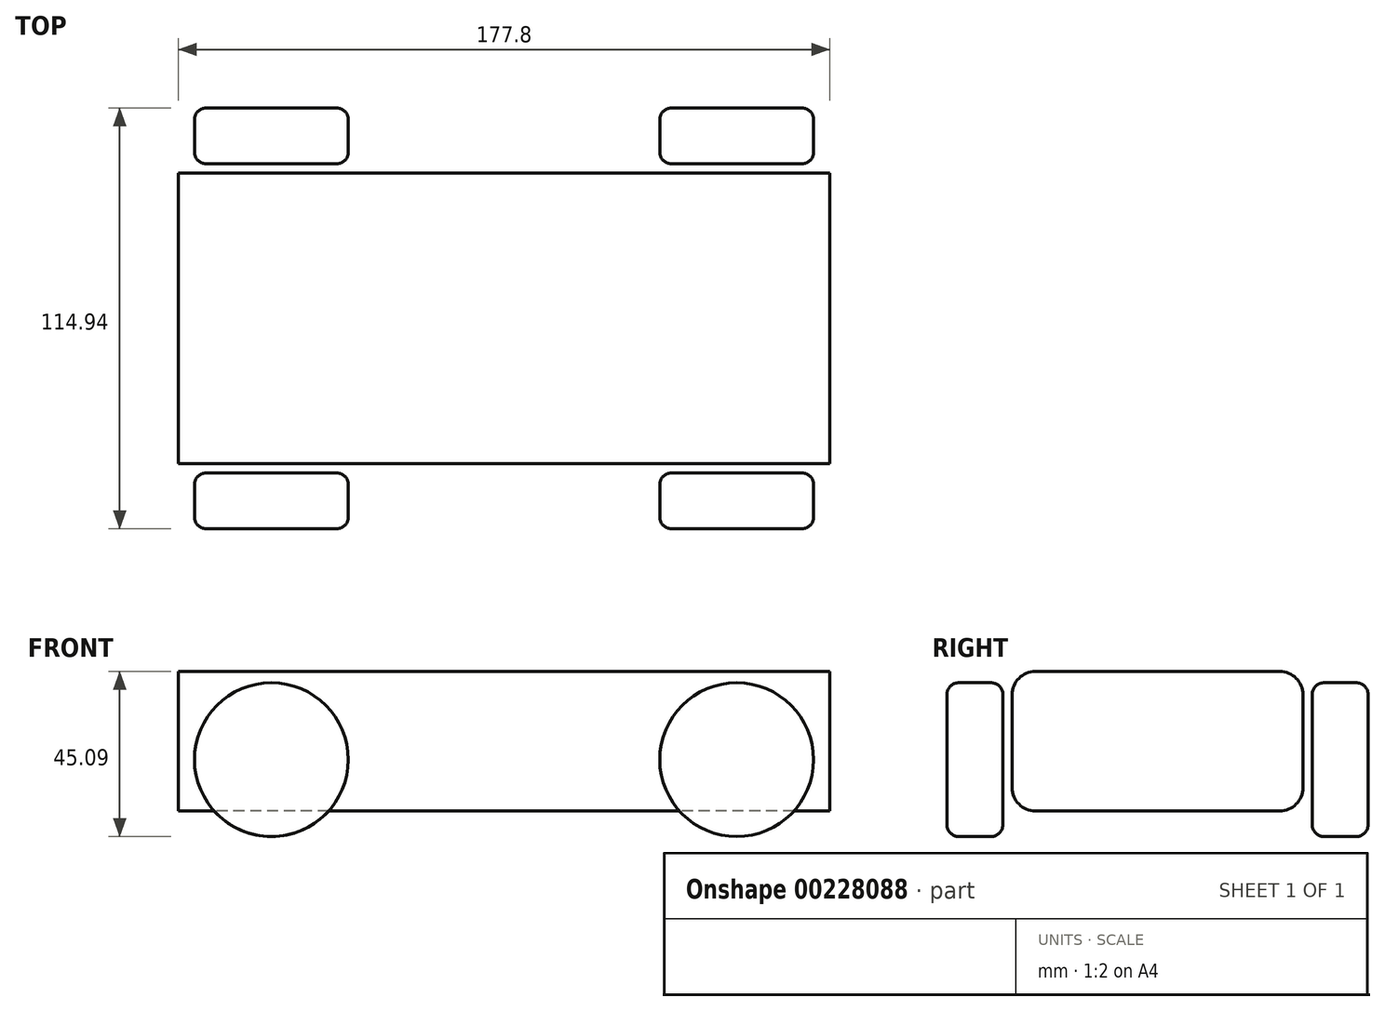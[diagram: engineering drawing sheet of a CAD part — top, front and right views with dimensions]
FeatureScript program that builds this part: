
annotation { "Feature Type Name" : "Feature", "Feature Type Description" : "" }
export const myFeature = defineFeature(function(context is Context, id is Id, definition is map)
    precondition{}
    {
        {
            var Q0;
            Q0=qCreatedBy(makeId("Front.planeOp"),FACE);
            var sketch = newSketch(context, id + "F0", { "sketchPlane" : qUnion([Q0])});
            skLineSegment(sketch, "E0.bottom", {"start": v(88.9, 19.05) * mm, "end": v(-88.9, 19.05) * mm});
            skLineSegment(sketch, "E0.top", {"start": v(88.9, -19.05) * mm, "end": v(-88.9, -19.05) * mm});
            skLineSegment(sketch, "E0.left", {"start": v(88.9, 19.05) * mm, "end": v(88.9, -19.05) * mm});
            skLineSegment(sketch, "E0.right", {"start": v(-88.9, 19.05) * mm, "end": v(-88.9, -19.05) * mm});
            skPoint(sketch, "E0.middle", {"position": v(0, 0) * mm});
            skLineSegment(sketch, "E1", {"start": v(-95.98, -26.04) * mm, "end": v(99.46, -26.03) * mm, "construction": true});
            skCircle(sketch, "E2", {"center": v(63.5, -5.03) * mm, "radius": 21 * mm});
            skSolve(sketch);
        }
        {
            var Q0;
            Q0=qCreatedBy(makeId("Front.planeOp"),FACE);
            var sketch = newSketch(context, id + "F1", { "sketchPlane" : qUnion([Q0])});
            skLineSegment(sketch, "E3.0", {"start": v(88.9, 19.05) * mm, "end": v(-88.9, 19.05) * mm});
            skLineSegment(sketch, "E4.0", {"start": v(-88.9, 19.05) * mm, "end": v(-88.9, -19.05) * mm});
            skLineSegment(sketch, "E5.0", {"start": v(88.9, -19.05) * mm, "end": v(-88.9, -19.05) * mm});
            skLineSegment(sketch, "E6.0", {"start": v(88.9, 19.05) * mm, "end": v(88.9, -19.05) * mm});
            skSolve(sketch);
        }
        {
            var Q0;
            Q0 = qSketchRegion(id + "F1", true);
            extrude(context, id + "F2", {"entities" : qUnion([Q0]), "endBound" : BoundingType.SYMMETRIC, "depth" : 79.38 * mm});
        }
        {
            var Q0;
            Q0=makeQuery(id+"F2.opExtrude","CAP_FACE",FACE,{"disambiguationData":[OSD([sQuery(id+"F1.wireOp",EDGE,"E3.0"),sQuery(id+"F1.wireOp",EDGE,"E4.0"),sQuery(id+"F1.wireOp",EDGE,"E5.0"),sQuery(id+"F1.wireOp",EDGE,"E6.0")])],"isStart":false});
            cPlane(context, id + "F3", {"entities" : qUnion([Q0]), "cplaneType" : CPlaneType.OFFSET, "offset" : 2.54 * mm, "width" : 152.4 * mm, "height" : 152.4 * mm});
        }
        {
            var Q0;
            Q0=qCreatedBy(id+"F3.planeOp",FACE);
            var sketch = newSketch(context, id + "F4", { "sketchPlane" : qUnion([Q0])});
            skCircle(sketch, "E7.0", {"center": v(63.5, -5.03) * mm, "radius": 21 * mm});
            skSolve(sketch);
        }
        {
            var Q0;
            Q0 = qSketchRegion(id + "F4", true);
            var Q1;
            Q1 = qConstructionFilter(qBodyType(qCreatedBy(id + "F4" ,EDGE), BodyType.WIRE), ConstructionObject.NO);
            extrude(context, id + "F5", {"entities" : qUnion([Q0]), "surfaceEntities" : qUnion([Q1]), "depth" : 15.24 * mm});
        }
        {
            var Q0;
            Q0=makeQuery(id+"F2.opExtrude","CAP_EDGE",EDGE,{"disambiguationData":[OSD([sQuery(id+"F1.wireOp",EDGE,"E3.0")])],"isStart":false});
            fillet(context, id + "F6", {"entities" : qUnion([Q0]), "radius" : 6.35 * mm, "tangentPropagation" : true, "allowEdgeOverflow" : false});
        }
        {
            var Q0;
            Q0=makeQuery(id+"F5.opExtrude","CAP_EDGE",EDGE,{"disambiguationData":[OSD([sQuery(id+"F4.wireOp",EDGE,"E7.0")])],"isStart":false});
            fillet(context, id + "F7", {"entities" : qUnion([Q0]), "radius" : 3.17 * mm, "tangentPropagation" : true, "allowEdgeOverflow" : false});
        }
        {
            var Q0;
            Q0=makeQuery(id+"F5.opExtrude","CAP_EDGE",EDGE,{"disambiguationData":[OSD([sQuery(id+"F4.wireOp",EDGE,"E7.0")])],"isStart":true});
            fillet(context, id + "F8", {"entities" : qUnion([Q0]), "radius" : 3.17 * mm, "tangentPropagation" : true, "allowEdgeOverflow" : false});
        }
        {
            var Q0;
            Q0=makeQuery(id+"F5.opExtrude","SWEPT_BODY",BODY,{"disambiguationData":[OSD([sQuery(id+"F4.wireOp",EDGE,"E7.0")])]});
            var Q1;
            Q1=qCreatedBy(makeId("Front.planeOp"),FACE);
            mirror(context, id + "F9", {"entities" : qUnion([Q0]), "mirrorPlane" : qUnion([Q1])});
        }
        {
            var Q0;
            Q0=makeQuery(id+"F2.opExtrude","CAP_EDGE",EDGE,{"disambiguationData":[OSD([sQuery(id+"F1.wireOp",EDGE,"E5.0")])],"isStart":false});
            var Q1;
            Q1=makeQuery(id+"F2.opExtrude","CAP_EDGE",EDGE,{"disambiguationData":[OSD([sQuery(id+"F1.wireOp",EDGE,"E3.0")])],"isStart":true});
            fillet(context, id + "F10", {"entities" : qUnion([Q0, Q1]), "radius" : 6.35 * mm, "tangentPropagation" : true, "allowEdgeOverflow" : false});
        }
        {
            var Q0;
            Q0=makeQuery(id+"F2.opExtrude","CAP_EDGE",EDGE,{"disambiguationData":[OSD([sQuery(id+"F1.wireOp",EDGE,"E5.0")])],"isStart":true});
            fillet(context, id + "F11", {"entities" : qUnion([Q0]), "radius" : 6.35 * mm, "tangentPropagation" : true, "allowEdgeOverflow" : false});
        }
        {
            var Q0;
            Q0=makeQuery(id+"F5.opExtrude","SWEPT_BODY",BODY,{"disambiguationData":[OSD([sQuery(id+"F4.wireOp",EDGE,"E7.0")])]});
            var Q1;
            Q1=makeQuery(id+"F9.opPattern","COPY",BODY,{"derivedFrom":makeQuery(id+"F5.opExtrude","SWEPT_BODY",BODY,{"disambiguationData":[OSD([sQuery(id+"F4.wireOp",EDGE,"E7.0")])]}),"instanceName":"1"});
            var Q2;
            Q2=qCreatedBy(makeId("Right.planeOp"),FACE);
            mirror(context, id + "F12", {"entities" : qUnion([Q0, Q1]), "mirrorPlane" : qUnion([Q2])});
        }
    });
